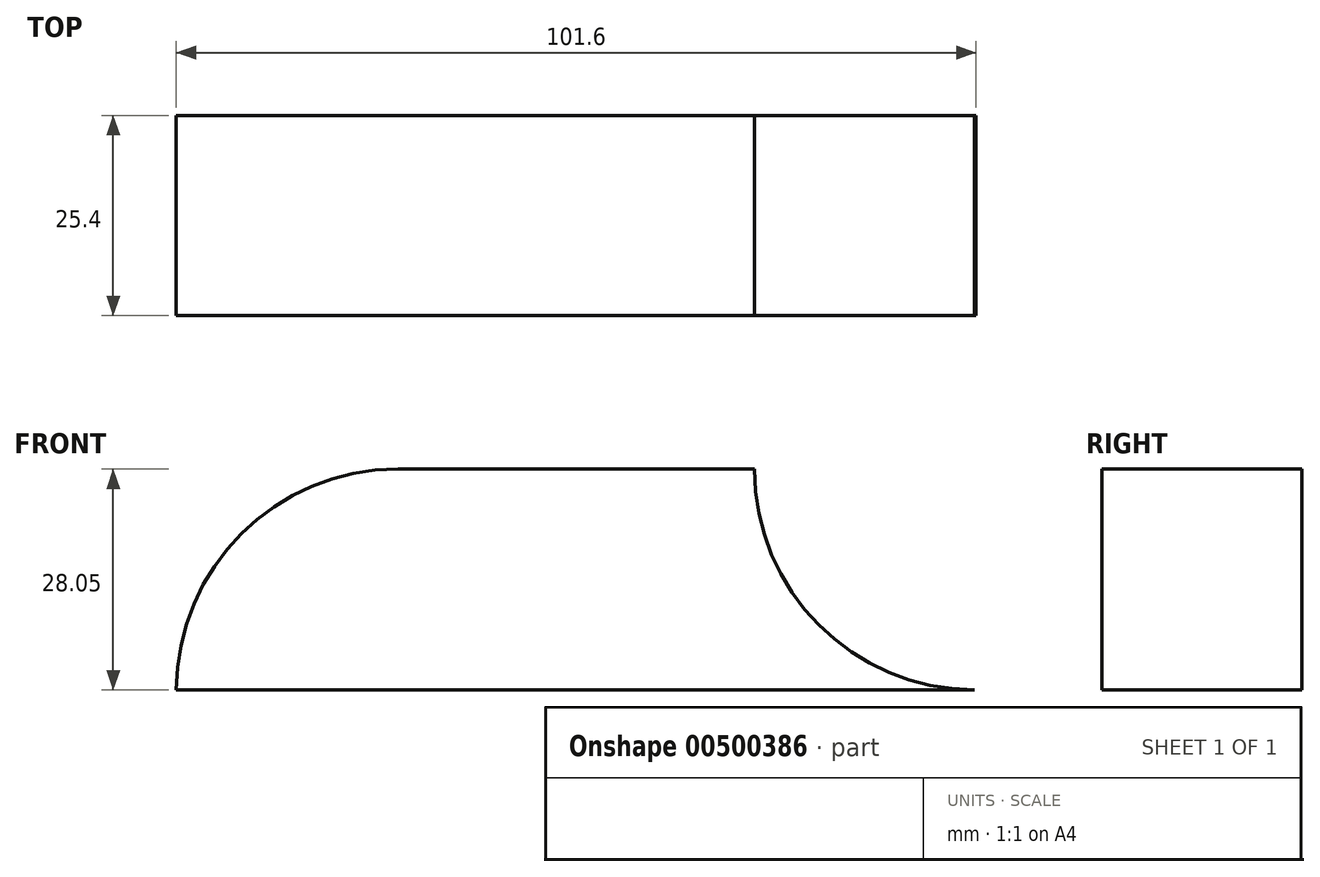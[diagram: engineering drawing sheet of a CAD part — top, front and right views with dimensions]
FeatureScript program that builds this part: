
annotation { "Feature Type Name" : "Feature", "Feature Type Description" : "" }
export const myFeature = defineFeature(function(context is Context, id is Id, definition is map)
    precondition{}
    {
        {
            var Q0;
            Q0=qCreatedBy(makeId("Front.planeOp"),FACE);
            var sketch = newSketch(context, id + "F0", { "sketchPlane" : qUnion([Q0])});
            skLineSegment(sketch, "E0.bottom", {"start": v(50.8, 19.05) * mm, "end": v(-50.8, 19.05) * mm});
            skLineSegment(sketch, "E0.top", {"start": v(50.8, -19.05) * mm, "end": v(-50.8, -19.05) * mm});
            skLineSegment(sketch, "E0.left", {"start": v(50.8, 19.05) * mm, "end": v(50.8, -19.05) * mm});
            skLineSegment(sketch, "E0.right", {"start": v(-50.8, 19.05) * mm, "end": v(-50.8, -19.05) * mm});
            skPoint(sketch, "E0.middle", {"position": v(0, 0) * mm});
            skLineSegment(sketch, "E1.bottom", {"start": v(22.65, 47.1) * mm, "end": v(-22.65, 47.1) * mm});
            skLineSegment(sketch, "E1.top", {"start": v(22.65, 69.65) * mm, "end": v(-22.65, 69.65) * mm});
            skLineSegment(sketch, "E1.left", {"start": v(22.65, 47.1) * mm, "end": v(22.65, 69.65) * mm});
            skLineSegment(sketch, "E1.right", {"start": v(-22.65, 47.1) * mm, "end": v(-22.65, 69.65) * mm});
            skPoint(sketch, "E1.middle", {"position": v(0, 58.37) * mm});
            skArc(sketch, "E2", {"start": v(-22.65, 47.1) * mm, "mid": v(-42.52, 38.9) * mm, "end": v(-50.8, 19.05) * mm});
            skArc(sketch, "E3", {"start": v(22.65, 47.1) * mm, "mid": v(30.9, 27.23) * mm, "end": v(50.8, 19.05) * mm});
            skSolve(sketch);
        }
        {
            var Q0;
            {var subQ1=sQuery(id+"F0.wireOp",EDGE,"E0.bottom");Q0=makeQuery(id+"F0.imprint","IMPRINT",FACE,{"disambiguationData":[TD([[makeQuery(id+"F0.imprint","IMPRINT",EDGE,{"derivedFrom":subQ1}),1.0]])]});}
            var Q1;
            {var subQ0=sQuery(id+"F0.wireOp",EDGE,"E0.bottom");Q1=makeQuery(id+"F0.imprint","IMPRINT",FACE,{"disambiguationData":[TD([[makeQuery(id+"F0.imprint","IMPRINT",EDGE,{"derivedFrom":subQ0}),-1.0]])]});}
            extrude(context, id + "F1", {"entities" : qUnion([Q0, Q1]), "depth" : 25.4 * mm});
        }
    });
